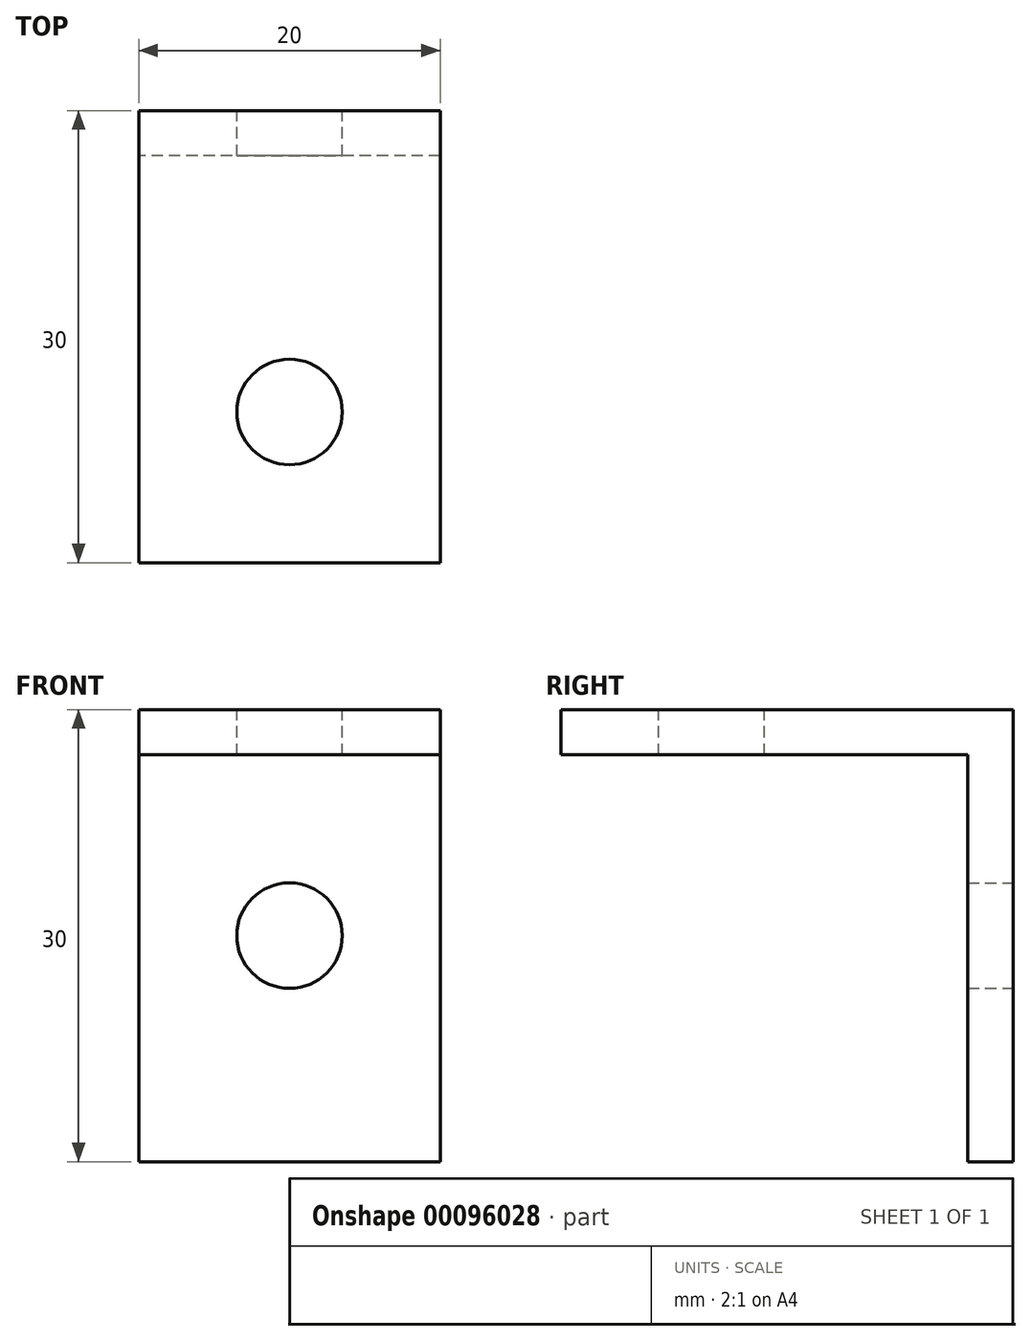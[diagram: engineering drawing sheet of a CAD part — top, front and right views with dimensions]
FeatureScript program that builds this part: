
annotation { "Feature Type Name" : "Feature", "Feature Type Description" : "" }
export const myFeature = defineFeature(function(context is Context, id is Id, definition is map)
    precondition{}
    {
        {
            var Q0;
            Q0=qCreatedBy(makeId("Right.planeOp"),FACE);
            var sketch = newSketch(context, id + "F0", { "sketchPlane" : qUnion([Q0])});
            skLineSegment(sketch, "E0", {"start": v(-30, 0) * mm, "end": v(0, 0) * mm});
            skLineSegment(sketch, "E1", {"start": v(0, 0) * mm, "end": v(0, -30) * mm});
            skLineSegment(sketch, "E2.0", {"start": v(-3, -3) * mm, "end": v(-3, -30) * mm});
            skLineSegment(sketch, "E2.1", {"start": v(-30, -3) * mm, "end": v(-3, -3) * mm});
            skLineSegment(sketch, "E3", {"start": v(-30, 0) * mm, "end": v(-30, -3) * mm});
            skLineSegment(sketch, "E4", {"start": v(-3, -30) * mm, "end": v(0, -30) * mm});
            skSolve(sketch);
        }
        {
            var Q0;
            Q0 = qSketchRegion(id + "F0", true);
            extrude(context, id + "F1", {"entities" : qUnion([Q0]), "endBound" : BoundingType.SYMMETRIC, "depth" : 20 * mm});
        }
        {
            var Q0;
            Q0=makeQuery(id+"F1.opExtrude","SWEPT_FACE",FACE,{"disambiguationData":[OSD([sQuery(id+"F0.wireOp",EDGE,"E1")])]});
            var sketch = newSketch(context, id + "F2", { "sketchPlane" : qUnion([Q0])});
            skCircle(sketch, "E5", {"center": v(0, -15) * mm, "radius": 3.5 * mm});
            skSolve(sketch);
        }
        {
            var Q0;
            Q0 = qSketchRegion(id + "F2", true);
            extrude(context, id + "F3", {"entities" : qUnion([Q0]), "operationType" : NewBodyOperationType.REMOVE, "endBound" : BoundingType.THROUGH_ALL, "oppositeDirection" : true, "depth" : 25 * mm});
        }
        {
            var Q0;
            Q0=makeQuery(id+"F1.opExtrude","SWEPT_FACE",FACE,{"disambiguationData":[OSD([sQuery(id+"F0.wireOp",EDGE,"E0")])]});
            var sketch = newSketch(context, id + "F4", { "sketchPlane" : qUnion([Q0])});
            skCircle(sketch, "E6", {"center": v(0, -20) * mm, "radius": 3.5 * mm});
            skSolve(sketch);
        }
        {
            var Q0;
            Q0 = qSketchRegion(id + "F4", true);
            extrude(context, id + "F5", {"entities" : qUnion([Q0]), "operationType" : NewBodyOperationType.REMOVE, "endBound" : BoundingType.THROUGH_ALL, "oppositeDirection" : true, "depth" : 25 * mm});
        }
    });
